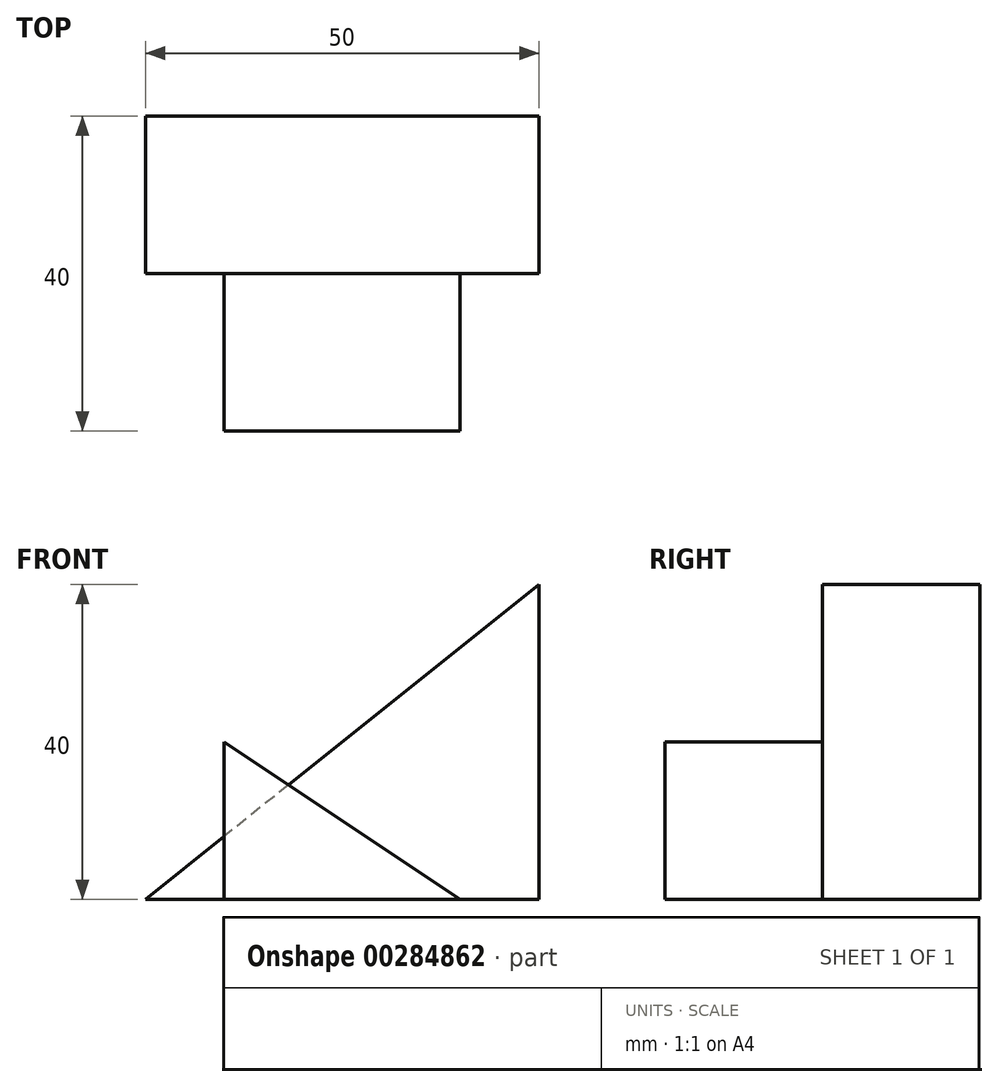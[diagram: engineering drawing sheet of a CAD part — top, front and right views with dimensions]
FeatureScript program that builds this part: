
annotation { "Feature Type Name" : "Feature", "Feature Type Description" : "" }
export const myFeature = defineFeature(function(context is Context, id is Id, definition is map)
    precondition{}
    {
        {
            var Q0;
            Q0=qCreatedBy(makeId("Front.planeOp"),FACE);
            var sketch = newSketch(context, id + "F0", { "sketchPlane" : qUnion([Q0])});
            skLineSegment(sketch, "E0.bottom", {"start": v(0, 0) * mm, "end": v(50, 0) * mm});
            skLineSegment(sketch, "E0.top", {"start": v(0, 40) * mm, "end": v(50, 40) * mm});
            skLineSegment(sketch, "E0.left", {"start": v(0, 0) * mm, "end": v(0, 40) * mm});
            skLineSegment(sketch, "E0.right", {"start": v(50, 0) * mm, "end": v(50, 40) * mm});
            skLineSegment(sketch, "E1", {"start": v(50, 40) * mm, "end": v(0, 0) * mm});
            skSolve(sketch);
        }
        {
            var Q0;
            Q0=makeQuery(id+"F0.imprint","IMPRINT",FACE,{"disambiguationData":[TD([[makeQuery(id+"F0.imprint","IMPRINT",EDGE,{"derivedFrom":sQuery(id+"F0.wireOp",EDGE,"E0.bottom")}),1.0]])]});
            extrude(context, id + "F1", {"entities" : qUnion([Q0]), "depth" : 20 * mm});
        }
        {
            var Q0;
            Q0=makeQuery(id+"F1.opExtrude","CAP_FACE",FACE,{"disambiguationData":[OSD([sQuery(id+"F0.wireOp",EDGE,"E0.bottom"),sQuery(id+"F0.wireOp",EDGE,"E0.top"),sQuery(id+"F0.wireOp",EDGE,"E0.left"),sQuery(id+"F0.wireOp",EDGE,"E0.right")])],"isStart":false});
            var sketch = newSketch(context, id + "F2", { "sketchPlane" : qUnion([Q0])});
            skLineSegment(sketch, "E2.bottom", {"start": v(10, 0) * mm, "end": v(40, 0) * mm});
            skLineSegment(sketch, "E2.top", {"start": v(10, 20) * mm, "end": v(40, 20) * mm});
            skLineSegment(sketch, "E2.left", {"start": v(10, 0) * mm, "end": v(10, 20) * mm});
            skLineSegment(sketch, "E2.right", {"start": v(40, 0) * mm, "end": v(40, 20) * mm});
            skLineSegment(sketch, "E3", {"start": v(10, 20) * mm, "end": v(40, 0) * mm});
            skSolve(sketch);
        }
        {
            var Q0;
            Q0=makeQuery(id+"F2.imprint","IMPRINT",FACE,{"disambiguationData":[TD([[makeQuery(id+"F2.imprint","IMPRINT",EDGE,{"derivedFrom":sQuery(id+"F2.wireOp",EDGE,"E2.bottom")}),1.0]])]});
            var Q1;
            {var subQ1=sQuery(id+"F2.wireOp",EDGE,"E2.left");var subQ3=makeQuery(id+"F1.opExtrude","CAP_EDGE",EDGE,{"disambiguationData":[OSD([sQuery(id+"F0.wireOp",EDGE,"E1")])],"isStart":false});var subQ4=makeQuery(id+"F2.imprint","INTERSECT",VERTEX,{"derivedFrom":[subQ3,subQ1]});Q1=makeQuery(id+"F2.imprint","IMPRINT",FACE,{"disambiguationData":[TD([[makeQuery(id+"F2.imprint","IMPRINT",EDGE,{"disambiguationData":[TD([[subQ4,1.0]])],"derivedFrom":subQ3}),-1.0]])]});}
            extrude(context, id + "F3", {"entities" : qUnion([Q0, Q1]), "operationType" : NewBodyOperationType.ADD, "depth" : 20 * mm});
        }
    });
